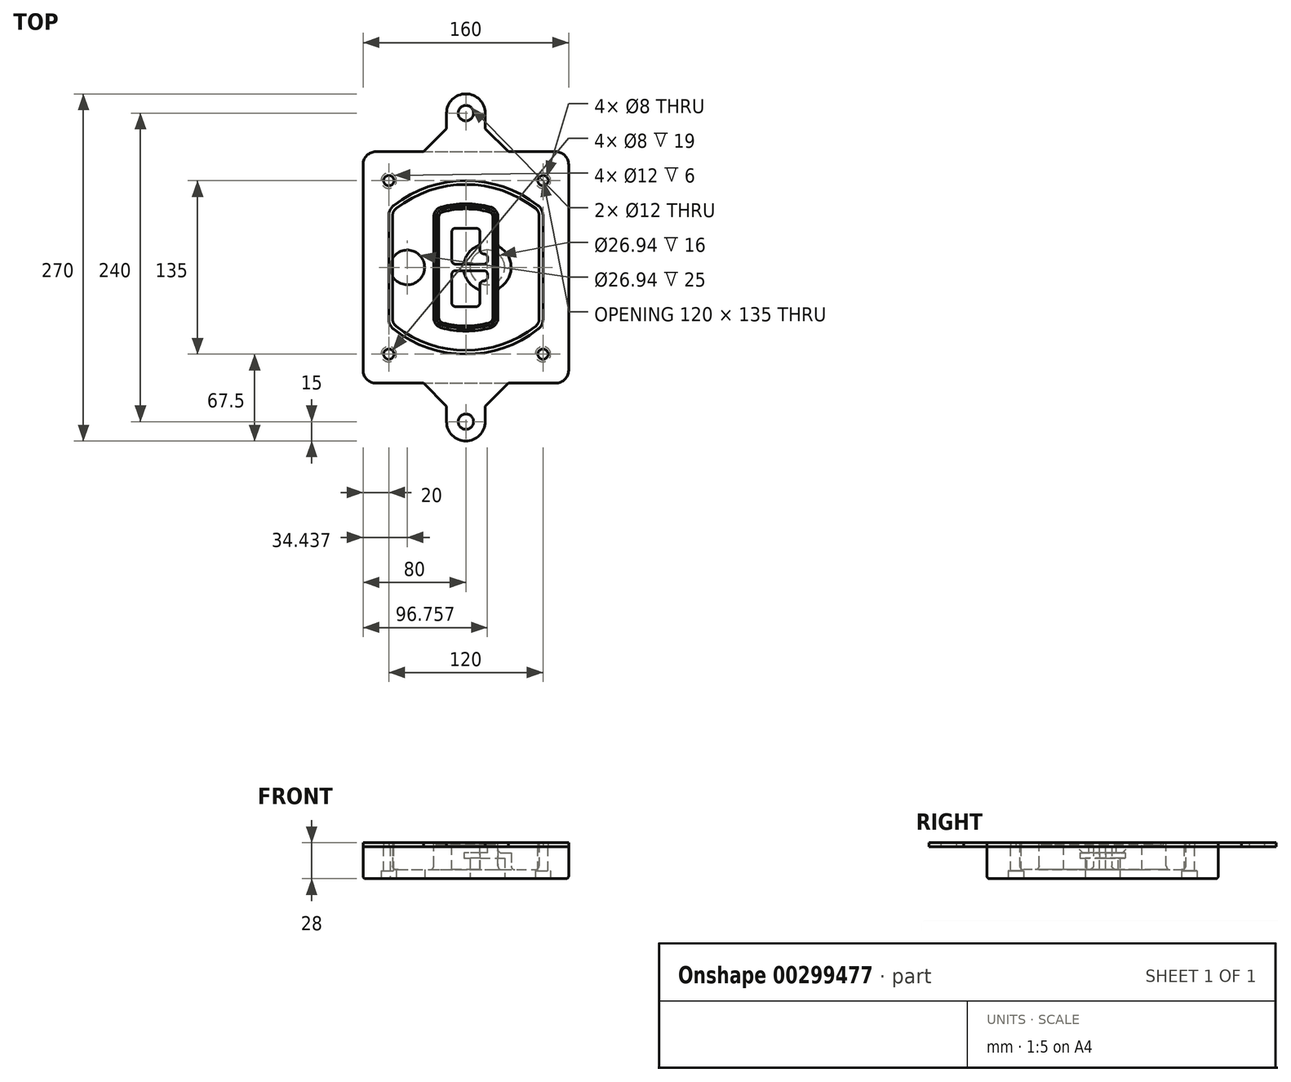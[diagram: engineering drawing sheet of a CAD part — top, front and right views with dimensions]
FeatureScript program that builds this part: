
annotation { "Feature Type Name" : "Feature", "Feature Type Description" : "" }
export const myFeature = defineFeature(function(context is Context, id is Id, definition is map)
    precondition{}
    {
        {
            var Q0;
            Q0=qCreatedBy(makeId("Top.planeOp"),FACE);
            var sketch = newSketch(context, id + "F0", { "sketchPlane" : qUnion([Q0])});
            skPoint(sketch, "E0.rect.middle", {"position": v(0, 0) * mm});
            skLineSegment(sketch, "E1.bottom", {"start": v(-70, -90) * mm, "end": v(70, -90) * mm});
            skLineSegment(sketch, "E1.top", {"start": v(-70, 90) * mm, "end": v(70, 90) * mm});
            skLineSegment(sketch, "E1.left", {"start": v(-80, -80) * mm, "end": v(-80, 80) * mm});
            skLineSegment(sketch, "E1.right", {"start": v(80, -80) * mm, "end": v(80, 80) * mm});
            skLineSegment(sketch, "E2", {"start": v(-80, 90) * mm, "end": v(80, -90) * mm, "construction": true});
            skLineSegment(sketch, "E3", {"start": v(80, 90) * mm, "end": v(-80, -90) * mm, "construction": true});
            skCircle(sketch, "E4", {"center": v(-60, 67.5) * mm, "radius": 4 * mm});
            skCircle(sketch, "E5", {"center": v(60, 67.5) * mm, "radius": 4 * mm});
            skCircle(sketch, "E6", {"center": v(60, -67.5) * mm, "radius": 4 * mm});
            skCircle(sketch, "E7", {"center": v(-60, -67.5) * mm, "radius": 4 * mm});
            skLineSegment(sketch, "E8", {"start": v(-60, 67.5) * mm, "end": v(60, 67.5) * mm, "construction": true});
            skLineSegment(sketch, "E9", {"start": v(60, 67.5) * mm, "end": v(60, -67.5) * mm, "construction": true});
            skLineSegment(sketch, "E10", {"start": v(60, -67.5) * mm, "end": v(-60, -67.5) * mm, "construction": true});
            skLineSegment(sketch, "E11", {"start": v(-60, -67.5) * mm, "end": v(-60, 67.5) * mm, "construction": true});
            skLineSegment(sketch, "E12", {"start": v(-60, 40.3) * mm, "end": v(-60, -40.3) * mm});
            skLineSegment(sketch, "E13", {"start": v(60, 40.3) * mm, "end": v(60, -40.3) * mm});
            skArc(sketch, "E14", {"start": v(56.15, 48.18) * mm, "mid": v(0, 67.5) * mm, "end": v(-56.15, 48.18) * mm});
            skArc(sketch, "E15", {"start": v(-56.15, -48.18) * mm, "mid": v(0, -67.5) * mm, "end": v(56.15, -48.18) * mm});
            skLineSegment(sketch, "E16", {"start": v(-60, 0) * mm, "end": v(60, 0) * mm, "construction": true});
            skPoint(sketch, "E17.visualSharp", {"position": v(-60, -45) * mm});
            skArc(sketch, "E17.filletArc", {"start": v(-60, -40.3) * mm, "mid": v(-58.99, -44.68) * mm, "end": v(-56.15, -48.18) * mm});
            skPoint(sketch, "E18.visualSharp", {"position": v(-60, 45) * mm});
            skArc(sketch, "E18.filletArc", {"start": v(-56.15, 48.18) * mm, "mid": v(-58.99, 44.68) * mm, "end": v(-60, 40.3) * mm});
            skPoint(sketch, "E19.visualSharp", {"position": v(60, 45) * mm});
            skArc(sketch, "E19.filletArc", {"start": v(60, 40.3) * mm, "mid": v(58.99, 44.68) * mm, "end": v(56.15, 48.18) * mm});
            skPoint(sketch, "E20.visualSharp", {"position": v(60, -45) * mm});
            skArc(sketch, "E20.filletArc", {"start": v(56.15, -48.18) * mm, "mid": v(58.99, -44.68) * mm, "end": v(60, -40.3) * mm});
            skPoint(sketch, "E21.visualSharp", {"position": v(-80, 90) * mm});
            skArc(sketch, "E21.filletArc", {"start": v(-70, 90) * mm, "mid": v(-77.07, 87.07) * mm, "end": v(-80, 80) * mm});
            skPoint(sketch, "E22.visualSharp", {"position": v(80, 90) * mm});
            skArc(sketch, "E22.filletArc", {"start": v(80, 80) * mm, "mid": v(77.07, 87.07) * mm, "end": v(70, 90) * mm});
            skPoint(sketch, "E23.visualSharp", {"position": v(80, -90) * mm});
            skArc(sketch, "E23.filletArc", {"start": v(70, -90) * mm, "mid": v(77.07, -87.07) * mm, "end": v(80, -80) * mm});
            skPoint(sketch, "E24.visualSharp", {"position": v(-80, -90) * mm});
            skArc(sketch, "E24.filletArc", {"start": v(-80, -80) * mm, "mid": v(-77.07, -87.07) * mm, "end": v(-70, -90) * mm});
            skArc(sketch, "E25.0", {"start": v(57, 40.3) * mm, "mid": v(56.3, 43.36) * mm, "end": v(54.3, 45.81) * mm});
            skLineSegment(sketch, "E25.1", {"start": v(57, 40.3) * mm, "end": v(57, -40.3) * mm});
            skArc(sketch, "E25.2", {"start": v(54.3, -45.81) * mm, "mid": v(56.3, -43.36) * mm, "end": v(57, -40.3) * mm});
            skArc(sketch, "E25.3", {"start": v(-54.3, -45.81) * mm, "mid": v(0, -64.5) * mm, "end": v(54.3, -45.81) * mm});
            skArc(sketch, "E25.4", {"start": v(-57, -40.3) * mm, "mid": v(-56.3, -43.36) * mm, "end": v(-54.3, -45.81) * mm});
            skArc(sketch, "E25.5", {"start": v(54.3, 45.81) * mm, "mid": v(0, 64.5) * mm, "end": v(-54.3, 45.81) * mm});
            skLineSegment(sketch, "E25.6", {"start": v(-57, 40.3) * mm, "end": v(-57, -40.3) * mm});
            skArc(sketch, "E25.7", {"start": v(-54.3, 45.81) * mm, "mid": v(-56.3, 43.36) * mm, "end": v(-57, 40.3) * mm});
            skArc(sketch, "E26.0", {"start": v(-58.62, 51.33) * mm, "mid": v(-62.58, 46.43) * mm, "end": v(-64, 40.3) * mm});
            skArc(sketch, "E26.1", {"start": v(58.62, 51.33) * mm, "mid": v(0, 71.5) * mm, "end": v(-58.62, 51.33) * mm});
            skArc(sketch, "E26.2", {"start": v(64, 40.3) * mm, "mid": v(62.58, 46.43) * mm, "end": v(58.62, 51.33) * mm});
            skLineSegment(sketch, "E26.3", {"start": v(64, 40.3) * mm, "end": v(64, -40.3) * mm});
            skArc(sketch, "E26.4", {"start": v(58.62, -51.33) * mm, "mid": v(62.58, -46.43) * mm, "end": v(64, -40.3) * mm});
            skLineSegment(sketch, "E26.5", {"start": v(-64, 40.3) * mm, "end": v(-64, -40.3) * mm});
            skArc(sketch, "E26.6", {"start": v(-58.62, -51.33) * mm, "mid": v(0, -71.5) * mm, "end": v(58.62, -51.33) * mm});
            skArc(sketch, "E26.7", {"start": v(-64, -40.3) * mm, "mid": v(-62.58, -46.43) * mm, "end": v(-58.62, -51.33) * mm});
            skSolve(sketch);
        }
        {
            var Q0;
            Q0=makeQuery(id+"F0.imprint","IMPRINT",FACE,{"disambiguationData":[TD([[makeQuery(id+"F0.imprint","IMPRINT",EDGE,{"derivedFrom":sQuery(id+"F0.wireOp",EDGE,"E1.bottom")}),1.0]])]});
            var Q1;
            Q1=makeQuery(id+"F0.imprint","IMPRINT",FACE,{"disambiguationData":[TD([[makeQuery(id+"F0.imprint","IMPRINT",EDGE,{"derivedFrom":sQuery(id+"F0.wireOp",EDGE,"E12")}),1.0]])]});
            var Q2;
            Q2=makeQuery(id+"F0.imprint","IMPRINT",FACE,{"disambiguationData":[TD([[makeQuery(id+"F0.imprint","IMPRINT",EDGE,{"derivedFrom":sQuery(id+"F0.wireOp",EDGE,"E25.0")}),1.0]])]});
            var Q3;
            Q3=makeQuery(id+"F0.imprint","IMPRINT",FACE,{"disambiguationData":[TD([[makeQuery(id+"F0.imprint","IMPRINT",EDGE,{"derivedFrom":sQuery(id+"F0.wireOp",EDGE,"E12")}),-1.0]])]});
            extrude(context, id + "F1", {"entities" : qUnion([Q0, Q1, Q2, Q3]), "oppositeDirection" : true, "depth" : 25 * mm});
        }
        {
            var Q0;
            Q0=makeQuery(id+"F0.imprint","IMPRINT",FACE,{"disambiguationData":[TD([[makeQuery(id+"F0.imprint","IMPRINT",EDGE,{"derivedFrom":sQuery(id+"F0.wireOp",EDGE,"E12")}),1.0]])]});
            extrude(context, id + "F2", {"entities" : qUnion([Q0]), "operationType" : NewBodyOperationType.ADD, "depth" : 3 * mm});
        }
        {
            var Q0;
            Q0=makeQuery(id+"F0.imprint","IMPRINT",FACE,{"disambiguationData":[TD([[makeQuery(id+"F0.imprint","IMPRINT",EDGE,{"derivedFrom":sQuery(id+"F0.wireOp",EDGE,"E25.0")}),1.0]])]});
            extrude(context, id + "F3", {"entities" : qUnion([Q0]), "operationType" : NewBodyOperationType.REMOVE, "oppositeDirection" : true, "depth" : 18 * mm});
        }
        {
            var Q0;
            Q0=makeQuery(id+"F2.opExtrude","CAP_FACE",FACE,{"disambiguationData":[OSD([sQuery(id+"F0.wireOp",EDGE,"E12"),sQuery(id+"F0.wireOp",EDGE,"E13"),sQuery(id+"F0.wireOp",EDGE,"E14"),sQuery(id+"F0.wireOp",EDGE,"E15"),sQuery(id+"F0.wireOp",EDGE,"E17.filletArc"),sQuery(id+"F0.wireOp",EDGE,"E18.filletArc"),sQuery(id+"F0.wireOp",EDGE,"E19.filletArc"),sQuery(id+"F0.wireOp",EDGE,"E20.filletArc"),sQuery(id+"F0.wireOp",EDGE,"E25.0"),sQuery(id+"F0.wireOp",EDGE,"E25.1"),sQuery(id+"F0.wireOp",EDGE,"E25.2"),sQuery(id+"F0.wireOp",EDGE,"E25.3"),sQuery(id+"F0.wireOp",EDGE,"E25.4"),sQuery(id+"F0.wireOp",EDGE,"E25.5"),sQuery(id+"F0.wireOp",EDGE,"E25.6"),sQuery(id+"F0.wireOp",EDGE,"E25.7")])],"isStart":false});
            var sketch = newSketch(context, id + "F4", { "sketchPlane" : qUnion([Q0])});
            skArc(sketch, "E27.0", {"start": v(-19.08, -46.97) * mm, "mid": v(0, -49.5) * mm, "end": v(19.08, -46.97) * mm});
            skArc(sketch, "E28.0", {"start": v(19.08, 46.97) * mm, "mid": v(0, 49.5) * mm, "end": v(-19.08, 46.97) * mm});
            skLineSegment(sketch, "E29", {"start": v(-25, 39.25) * mm, "end": v(-25, -39.25) * mm});
            skLineSegment(sketch, "E30", {"start": v(25, 39.25) * mm, "end": v(25, -39.25) * mm});
            skLineSegment(sketch, "E31", {"start": v(-25, 45.1) * mm, "end": v(25, 45.1) * mm, "construction": true});
            skLineSegment(sketch, "E32", {"start": v(-25, -45.1) * mm, "end": v(25, -45.1) * mm, "construction": true});
            skPoint(sketch, "E33.visualSharp", {"position": v(-25, 45.1) * mm});
            skArc(sketch, "E33.filletArc", {"start": v(-19.08, 46.97) * mm, "mid": v(-23.35, 44.11) * mm, "end": v(-25, 39.25) * mm});
            skPoint(sketch, "E34.visualSharp", {"position": v(25, 45.1) * mm});
            skArc(sketch, "E34.filletArc", {"start": v(25, 39.25) * mm, "mid": v(23.35, 44.11) * mm, "end": v(19.08, 46.97) * mm});
            skPoint(sketch, "E35.visualSharp", {"position": v(25, -45.1) * mm});
            skArc(sketch, "E35.filletArc", {"start": v(19.08, -46.97) * mm, "mid": v(23.35, -44.11) * mm, "end": v(25, -39.25) * mm});
            skPoint(sketch, "E36.visualSharp", {"position": v(-25, -45.1) * mm});
            skArc(sketch, "E36.filletArc", {"start": v(-25, -39.25) * mm, "mid": v(-23.35, -44.11) * mm, "end": v(-19.08, -46.97) * mm});
            skArc(sketch, "E37.0", {"start": v(54.3, 45.81) * mm, "mid": v(0, 64.5) * mm, "end": v(-54.3, 45.81) * mm});
            skArc(sketch, "E37.1", {"start": v(-54.3, 45.81) * mm, "mid": v(-56.3, 43.36) * mm, "end": v(-57, 40.3) * mm});
            skLineSegment(sketch, "E37.2", {"start": v(-57, 40.3) * mm, "end": v(-57, -40.3) * mm});
            skArc(sketch, "E37.3", {"start": v(-57, -40.3) * mm, "mid": v(-56.3, -43.36) * mm, "end": v(-54.3, -45.81) * mm});
            skArc(sketch, "E37.4", {"start": v(-54.3, -45.81) * mm, "mid": v(0, -64.5) * mm, "end": v(54.3, -45.81) * mm});
            skArc(sketch, "E37.5", {"start": v(54.3, -45.81) * mm, "mid": v(56.3, -43.36) * mm, "end": v(57, -40.3) * mm});
            skLineSegment(sketch, "E37.6", {"start": v(57, 40.3) * mm, "end": v(57, -40.3) * mm});
            skArc(sketch, "E37.7", {"start": v(57, 40.3) * mm, "mid": v(56.3, 43.36) * mm, "end": v(54.3, 45.81) * mm});
            skLineSegment(sketch, "E38.0", {"start": v(23, 39.25) * mm, "end": v(23, -39.25) * mm});
            skArc(sketch, "E38.1", {"start": v(18.56, -45.04) * mm, "mid": v(21.76, -42.9) * mm, "end": v(23, -39.25) * mm});
            skArc(sketch, "E38.2", {"start": v(-18.56, -45.04) * mm, "mid": v(0, -47.5) * mm, "end": v(18.56, -45.04) * mm});
            skArc(sketch, "E38.3", {"start": v(-23, -39.25) * mm, "mid": v(-21.76, -42.9) * mm, "end": v(-18.56, -45.04) * mm});
            skLineSegment(sketch, "E38.4", {"start": v(-23, 39.25) * mm, "end": v(-23, -39.25) * mm});
            skArc(sketch, "E38.5", {"start": v(23, 39.25) * mm, "mid": v(21.76, 42.9) * mm, "end": v(18.56, 45.04) * mm});
            skArc(sketch, "E38.6", {"start": v(-18.56, 45.04) * mm, "mid": v(-21.76, 42.9) * mm, "end": v(-23, 39.25) * mm});
            skArc(sketch, "E38.7", {"start": v(18.56, 45.04) * mm, "mid": v(0, 47.5) * mm, "end": v(-18.56, 45.04) * mm});
            skArc(sketch, "E39.0", {"start": v(21, 39.25) * mm, "mid": v(20.18, 41.68) * mm, "end": v(18.04, 43.1) * mm});
            skLineSegment(sketch, "E39.1", {"start": v(21, 39.25) * mm, "end": v(21, -39.25) * mm});
            skArc(sketch, "E39.2", {"start": v(18.04, -43.1) * mm, "mid": v(20.18, -41.68) * mm, "end": v(21, -39.25) * mm});
            skArc(sketch, "E39.3", {"start": v(-18.04, -43.1) * mm, "mid": v(0, -45.5) * mm, "end": v(18.04, -43.1) * mm});
            skArc(sketch, "E39.4", {"start": v(-21, -39.25) * mm, "mid": v(-20.18, -41.68) * mm, "end": v(-18.04, -43.1) * mm});
            skArc(sketch, "E39.5", {"start": v(18.04, 43.1) * mm, "mid": v(0, 45.5) * mm, "end": v(-18.04, 43.1) * mm});
            skLineSegment(sketch, "E39.6", {"start": v(-21, 39.25) * mm, "end": v(-21, -39.25) * mm});
            skArc(sketch, "E39.7", {"start": v(-18.04, 43.1) * mm, "mid": v(-20.18, 41.68) * mm, "end": v(-21, 39.25) * mm});
            skLineSegment(sketch, "E40", {"start": v(-25, 0) * mm, "end": v(25, 0) * mm, "construction": true});
            skLineSegment(sketch, "E41", {"start": v(-11, 5.5) * mm, "end": v(-11, 27.5) * mm});
            skLineSegment(sketch, "E42", {"start": v(-8, 30.5) * mm, "end": v(8, 30.5) * mm});
            skLineSegment(sketch, "E43", {"start": v(11, 27.5) * mm, "end": v(11, 13.5) * mm});
            skLineSegment(sketch, "E44", {"start": v(14, 10.5) * mm, "end": v(14, 10.5) * mm});
            skLineSegment(sketch, "E45", {"start": v(17, 7.5) * mm, "end": v(17, 5.5) * mm});
            skLineSegment(sketch, "E46", {"start": v(14, 2.5) * mm, "end": v(-8, 2.5) * mm});
            skPoint(sketch, "E47.visualSharp", {"position": v(-11, 30.5) * mm});
            skArc(sketch, "E47.filletArc", {"start": v(-8, 30.5) * mm, "mid": v(-10.12, 29.62) * mm, "end": v(-11, 27.5) * mm});
            skPoint(sketch, "E48.visualSharp", {"position": v(11, 30.5) * mm});
            skArc(sketch, "E48.filletArc", {"start": v(11, 27.5) * mm, "mid": v(10.12, 29.62) * mm, "end": v(8, 30.5) * mm});
            skPoint(sketch, "E49.visualSharp", {"position": v(11, 10.5) * mm});
            skArc(sketch, "E49.filletArc", {"start": v(11, 13.5) * mm, "mid": v(11.88, 11.38) * mm, "end": v(14, 10.5) * mm});
            skPoint(sketch, "E50.visualSharp", {"position": v(17, 10.5) * mm});
            skArc(sketch, "E50.filletArc", {"start": v(17, 7.5) * mm, "mid": v(16.12, 9.62) * mm, "end": v(14, 10.5) * mm});
            skPoint(sketch, "E51.visualSharp", {"position": v(17, 2.5) * mm});
            skArc(sketch, "E51.filletArc", {"start": v(14, 2.5) * mm, "mid": v(16.12, 3.38) * mm, "end": v(17, 5.5) * mm});
            skPoint(sketch, "E52.visualSharp", {"position": v(-11, 2.5) * mm});
            skArc(sketch, "E52.filletArc", {"start": v(-11, 5.5) * mm, "mid": v(-10.12, 3.38) * mm, "end": v(-8, 2.5) * mm});
            skLineSegment(sketch, "E53.0.MirrorCS", {"start": v(14, -2.5) * mm, "end": v(-8, -2.5) * mm});
            skArc(sketch, "E54.0.MirrorCS", {"start": v(-11, -5.5) * mm, "mid": v(-10.12, -3.38) * mm, "end": v(-8, -2.5) * mm});
            skLineSegment(sketch, "E55.0.MirrorCS", {"start": v(-11, -5.5) * mm, "end": v(-11, -27.5) * mm});
            skArc(sketch, "E56.0.MirrorCS", {"start": v(-8, -30.5) * mm, "mid": v(-10.12, -29.62) * mm, "end": v(-11, -27.5) * mm});
            skLineSegment(sketch, "E57.0.MirrorCS", {"start": v(-8, -30.5) * mm, "end": v(8, -30.5) * mm});
            skArc(sketch, "E58.0.MirrorCS", {"start": v(11, -27.5) * mm, "mid": v(10.12, -29.62) * mm, "end": v(8, -30.5) * mm});
            skLineSegment(sketch, "E59.0.MirrorCS", {"start": v(11, -27.5) * mm, "end": v(11, -13.5) * mm});
            skArc(sketch, "E60.0.MirrorCS", {"start": v(11, -13.5) * mm, "mid": v(11.88, -11.38) * mm, "end": v(14, -10.5) * mm});
            skArc(sketch, "E61.0.MirrorCS", {"start": v(17, -7.5) * mm, "mid": v(16.12, -9.62) * mm, "end": v(14, -10.5) * mm});
            skLineSegment(sketch, "E62.0.MirrorCS", {"start": v(17, -7.5) * mm, "end": v(17, -5.5) * mm});
            skArc(sketch, "E63.0.MirrorCS", {"start": v(14, -2.5) * mm, "mid": v(16.12, -3.38) * mm, "end": v(17, -5.5) * mm});
            skSolve(sketch);
        }
        {
            var Q0;
            Q0=makeQuery(id+"F4.imprint","IMPRINT",FACE,{"disambiguationData":[TD([[makeQuery(id+"F4.imprint","IMPRINT",EDGE,{"derivedFrom":sQuery(id+"F4.wireOp",EDGE,"E27.0")}),1.0]])]});
            var Q1;
            Q1=makeQuery(id+"F4.imprint","IMPRINT",FACE,{"disambiguationData":[TD([[makeQuery(id+"F4.imprint","IMPRINT",EDGE,{"derivedFrom":sQuery(id+"F4.wireOp",EDGE,"E38.0")}),-1.0]])]});
            var Q2;
            Q2=makeQuery(id+"F4.imprint","IMPRINT",FACE,{"disambiguationData":[TD([[makeQuery(id+"F4.imprint","IMPRINT",EDGE,{"derivedFrom":sQuery(id+"F4.wireOp",EDGE,"E39.0")}),1.0]])]});
            extrude(context, id + "F5", {"entities" : qUnion([Q0, Q1, Q2]), "operationType" : NewBodyOperationType.ADD, "endBound" : BoundingType.UP_TO_NEXT, "oppositeDirection" : true, "depth" : 25 * mm});
        }
        {
            var Q0;
            Q0=makeQuery(id+"F4.imprint","IMPRINT",FACE,{"disambiguationData":[TD([[makeQuery(id+"F4.imprint","IMPRINT",EDGE,{"derivedFrom":sQuery(id+"F4.wireOp",EDGE,"E38.0")}),-1.0]])]});
            extrude(context, id + "F6", {"entities" : qUnion([Q0]), "operationType" : NewBodyOperationType.REMOVE, "oppositeDirection" : true, "depth" : 2 * mm});
        }
        {
            var Q0;
            Q0=makeQuery(id+"F1.opExtrude","CAP_FACE",FACE,{"disambiguationData":[OSD([sQuery(id+"F0.wireOp",EDGE,"E1.bottom"),sQuery(id+"F0.wireOp",EDGE,"E1.top"),sQuery(id+"F0.wireOp",EDGE,"E1.left"),sQuery(id+"F0.wireOp",EDGE,"E1.right"),sQuery(id+"F0.wireOp",EDGE,"E4"),sQuery(id+"F0.wireOp",EDGE,"E5"),sQuery(id+"F0.wireOp",EDGE,"E6"),sQuery(id+"F0.wireOp",EDGE,"E7"),sQuery(id+"F0.wireOp",EDGE,"E21.filletArc"),sQuery(id+"F0.wireOp",EDGE,"E22.filletArc"),sQuery(id+"F0.wireOp",EDGE,"E23.filletArc"),sQuery(id+"F0.wireOp",EDGE,"E24.filletArc")])],"isStart":false});
            var sketch = newSketch(context, id + "F7", { "sketchPlane" : qUnion([Q0])});
            skCircle(sketch, "E64", {"center": v(16.76, 0) * mm, "radius": 13.47 * mm});
            skCircle(sketch, "E65", {"center": v(-45.56, 0) * mm, "radius": 13.47 * mm});
            skLineSegment(sketch, "E66", {"start": v(80, 0) * mm, "end": v(-80, 0) * mm});
            skCircle(sketch, "E67", {"center": v(16.76, 0) * mm, "radius": 18.47 * mm});
            skCircle(sketch, "E68", {"center": v(60, -67.5) * mm, "radius": 6 * mm});
            skCircle(sketch, "E69", {"center": v(-60, -67.5) * mm, "radius": 6 * mm});
            skCircle(sketch, "E70", {"center": v(-60, 67.5) * mm, "radius": 6 * mm});
            skCircle(sketch, "E71", {"center": v(60, 67.5) * mm, "radius": 6 * mm});
            skSolve(sketch);
        }
        {
            var Q0;
            {var subQ1=sQuery(id+"F7.wireOp",EDGE,"E66");var subQ4=sQuery(id+"F7.wireOp",EDGE,"E64");var subQ6=makeQuery(id+"F7.imprint","INTERSECT",VERTEX,{"disambiguationData":[OD(0.0)],"derivedFrom":[subQ4,subQ1]});Q0=makeQuery(id+"F7.imprint","IMPRINT",FACE,{"disambiguationData":[TD([[makeQuery(id+"F7.imprint","IMPRINT",EDGE,{"disambiguationData":[TD([[subQ6,-1.0]])],"derivedFrom":subQ4}),-1.0]])]});}
            var Q1;
            {var subQ0=sQuery(id+"F7.wireOp",EDGE,"E66");var subQ1=sQuery(id+"F7.wireOp",EDGE,"E64");var subQ3=makeQuery(id+"F7.imprint","INTERSECT",VERTEX,{"disambiguationData":[OD(0.0)],"derivedFrom":[subQ1,subQ0]});Q1=makeQuery(id+"F7.imprint","IMPRINT",FACE,{"disambiguationData":[TD([[makeQuery(id+"F7.imprint","IMPRINT",EDGE,{"disambiguationData":[TD([[subQ3,-1.0]])],"derivedFrom":subQ1}),1.0]])]});}
            var Q2;
            {var subQ0=sQuery(id+"F7.wireOp",EDGE,"E66");var subQ1=sQuery(id+"F7.wireOp",EDGE,"E64");var subQ3=makeQuery(id+"F7.imprint","INTERSECT",VERTEX,{"disambiguationData":[OD(0.0)],"derivedFrom":[subQ1,subQ0]});Q2=makeQuery(id+"F7.imprint","IMPRINT",FACE,{"disambiguationData":[TD([[makeQuery(id+"F7.imprint","IMPRINT",EDGE,{"disambiguationData":[TD([[subQ3,1.0]])],"derivedFrom":subQ1}),1.0]])]});}
            var Q3;
            {var subQ1=sQuery(id+"F7.wireOp",EDGE,"E66");var subQ4=sQuery(id+"F7.wireOp",EDGE,"E64");var subQ6=makeQuery(id+"F7.imprint","INTERSECT",VERTEX,{"disambiguationData":[OD(0.0)],"derivedFrom":[subQ4,subQ1]});Q3=makeQuery(id+"F7.imprint","IMPRINT",FACE,{"disambiguationData":[TD([[makeQuery(id+"F7.imprint","IMPRINT",EDGE,{"disambiguationData":[TD([[subQ6,1.0]])],"derivedFrom":subQ4}),-1.0]])]});}
            extrude(context, id + "F8", {"entities" : qUnion([Q0, Q1, Q2, Q3]), "operationType" : NewBodyOperationType.ADD, "oppositeDirection" : true, "depth" : 20 * mm});
        }
        {
            var Q0;
            {var subQ0=sQuery(id+"F7.wireOp",EDGE,"E66");var subQ1=sQuery(id+"F7.wireOp",EDGE,"E64");var subQ3=makeQuery(id+"F7.imprint","INTERSECT",VERTEX,{"disambiguationData":[OD(0.0)],"derivedFrom":[subQ1,subQ0]});Q0=makeQuery(id+"F7.imprint","IMPRINT",FACE,{"disambiguationData":[TD([[makeQuery(id+"F7.imprint","IMPRINT",EDGE,{"disambiguationData":[TD([[subQ3,-1.0]])],"derivedFrom":subQ1}),1.0]])]});}
            var Q1;
            {var subQ0=sQuery(id+"F7.wireOp",EDGE,"E66");var subQ1=sQuery(id+"F7.wireOp",EDGE,"E64");var subQ3=makeQuery(id+"F7.imprint","INTERSECT",VERTEX,{"disambiguationData":[OD(0.0)],"derivedFrom":[subQ1,subQ0]});Q1=makeQuery(id+"F7.imprint","IMPRINT",FACE,{"disambiguationData":[TD([[makeQuery(id+"F7.imprint","IMPRINT",EDGE,{"disambiguationData":[TD([[subQ3,1.0]])],"derivedFrom":subQ1}),1.0]])]});}
            extrude(context, id + "F9", {"entities" : qUnion([Q0, Q1]), "operationType" : NewBodyOperationType.REMOVE, "oppositeDirection" : true, "depth" : 16 * mm});
        }
        {
            var Q0;
            {var subQ0=sQuery(id+"F7.wireOp",EDGE,"E66");var subQ1=sQuery(id+"F7.wireOp",EDGE,"E65");var subQ3=makeQuery(id+"F7.imprint","INTERSECT",VERTEX,{"disambiguationData":[OD(0.0)],"derivedFrom":[subQ1,subQ0]});Q0=makeQuery(id+"F7.imprint","IMPRINT",FACE,{"disambiguationData":[TD([[makeQuery(id+"F7.imprint","IMPRINT",EDGE,{"disambiguationData":[TD([[subQ3,-1.0]])],"derivedFrom":subQ1}),1.0]])]});}
            var Q1;
            {var subQ0=sQuery(id+"F7.wireOp",EDGE,"E66");var subQ1=sQuery(id+"F7.wireOp",EDGE,"E65");var subQ3=makeQuery(id+"F7.imprint","INTERSECT",VERTEX,{"disambiguationData":[OD(0.0)],"derivedFrom":[subQ1,subQ0]});Q1=makeQuery(id+"F7.imprint","IMPRINT",FACE,{"disambiguationData":[TD([[makeQuery(id+"F7.imprint","IMPRINT",EDGE,{"disambiguationData":[TD([[subQ3,1.0]])],"derivedFrom":subQ1}),1.0]])]});}
            extrude(context, id + "F10", {"entities" : qUnion([Q0, Q1]), "operationType" : NewBodyOperationType.REMOVE, "oppositeDirection" : true, "depth" : 25 * mm});
        }
        {
            var Q0;
            Q0=makeQuery(id+"F7.imprint","IMPRINT",FACE,{"disambiguationData":[TD([[makeQuery(id+"F7.imprint","IMPRINT",EDGE,{"derivedFrom":sQuery(id+"F7.wireOp",EDGE,"E68")}),1.0]])]});
            var Q1;
            Q1=makeQuery(id+"F7.imprint","IMPRINT",FACE,{"disambiguationData":[TD([[makeQuery(id+"F7.imprint","IMPRINT",EDGE,{"derivedFrom":makeQuery(id+"F1.opExtrude","CAP_EDGE",EDGE,{"disambiguationData":[OSD([sQuery(id+"F0.wireOp",EDGE,"E5")])],"isStart":false})}),-1.0]])]});
            var Q2;
            Q2=makeQuery(id+"F7.imprint","IMPRINT",FACE,{"disambiguationData":[TD([[makeQuery(id+"F7.imprint","IMPRINT",EDGE,{"derivedFrom":sQuery(id+"F7.wireOp",EDGE,"E69")}),1.0]])]});
            var Q3;
            Q3=makeQuery(id+"F7.imprint","IMPRINT",FACE,{"disambiguationData":[TD([[makeQuery(id+"F7.imprint","IMPRINT",EDGE,{"derivedFrom":makeQuery(id+"F1.opExtrude","CAP_EDGE",EDGE,{"disambiguationData":[OSD([sQuery(id+"F0.wireOp",EDGE,"E4")])],"isStart":false})}),-1.0]])]});
            var Q4;
            Q4=makeQuery(id+"F7.imprint","IMPRINT",FACE,{"disambiguationData":[TD([[makeQuery(id+"F7.imprint","IMPRINT",EDGE,{"derivedFrom":sQuery(id+"F7.wireOp",EDGE,"E70")}),1.0]])]});
            var Q5;
            Q5=makeQuery(id+"F7.imprint","IMPRINT",FACE,{"disambiguationData":[TD([[makeQuery(id+"F7.imprint","IMPRINT",EDGE,{"derivedFrom":makeQuery(id+"F1.opExtrude","CAP_EDGE",EDGE,{"disambiguationData":[OSD([sQuery(id+"F0.wireOp",EDGE,"E7")])],"isStart":false})}),-1.0]])]});
            var Q6;
            Q6=makeQuery(id+"F7.imprint","IMPRINT",FACE,{"disambiguationData":[TD([[makeQuery(id+"F7.imprint","IMPRINT",EDGE,{"derivedFrom":sQuery(id+"F7.wireOp",EDGE,"E71")}),1.0]])]});
            var Q7;
            Q7=makeQuery(id+"F7.imprint","IMPRINT",FACE,{"disambiguationData":[TD([[makeQuery(id+"F7.imprint","IMPRINT",EDGE,{"derivedFrom":makeQuery(id+"F1.opExtrude","CAP_EDGE",EDGE,{"disambiguationData":[OSD([sQuery(id+"F0.wireOp",EDGE,"E6")])],"isStart":false})}),-1.0]])]});
            extrude(context, id + "F11", {"entities" : qUnion([Q0, Q1, Q2, Q3, Q4, Q5, Q6, Q7]), "operationType" : NewBodyOperationType.REMOVE, "oppositeDirection" : true, "depth" : 6 * mm});
        }
        {
            var Q0;
            Q0=makeQuery(id+"F9.boolean.opBoolean","COPY",FACE,{"derivedFrom":makeQuery(id+"F9.opExtrude","CAP_FACE",FACE,{"disambiguationData":[OSD([sQuery(id+"F7.wireOp",EDGE,"E64")])],"isStart":false})});
            var sketch = newSketch(context, id + "F12", { "sketchPlane" : qUnion([Q0])});
            skArc(sketch, "E72.0", {"start": v(11, 17.55) * mm, "mid": v(2.57, 11.82) * mm, "end": v(-1.54, 2.5) * mm});
            skArc(sketch, "E72.1", {"start": v(-1.54, -2.5) * mm, "mid": v(2.57, -11.82) * mm, "end": v(11, -17.55) * mm});
            skLineSegment(sketch, "E73", {"start": v(-1.54, -2.5) * mm, "end": v(14, -2.5) * mm});
            skLineSegment(sketch, "E74.0", {"start": v(14, 2.5) * mm, "end": v(-1.54, 2.5) * mm});
            skArc(sketch, "E74.1", {"start": v(14, 2.5) * mm, "mid": v(16.12, 3.38) * mm, "end": v(17, 5.5) * mm});
            skLineSegment(sketch, "E74.2", {"start": v(17, 7.5) * mm, "end": v(17, 5.5) * mm});
            skArc(sketch, "E74.3", {"start": v(17, 7.5) * mm, "mid": v(16.12, 9.62) * mm, "end": v(14, 10.5) * mm});
            skArc(sketch, "E74.4", {"start": v(11, 13.5) * mm, "mid": v(11.88, 11.38) * mm, "end": v(14, 10.5) * mm});
            skLineSegment(sketch, "E74.5", {"start": v(11, 17.55) * mm, "end": v(11, 13.5) * mm});
            skLineSegment(sketch, "E74.7", {"start": v(14, -2.5) * mm, "end": v(-1.54, -2.5) * mm});
            skArc(sketch, "E74.8", {"start": v(14, -2.5) * mm, "mid": v(16.12, -3.38) * mm, "end": v(17, -5.5) * mm});
            skLineSegment(sketch, "E74.9", {"start": v(17, -7.5) * mm, "end": v(17, -5.5) * mm});
            skArc(sketch, "E74.10", {"start": v(17, -7.5) * mm, "mid": v(16.12, -9.62) * mm, "end": v(14, -10.5) * mm});
            skArc(sketch, "E74.11", {"start": v(11, -13.5) * mm, "mid": v(11.88, -11.38) * mm, "end": v(14, -10.5) * mm});
            skLineSegment(sketch, "E74.12", {"start": v(11, -17.55) * mm, "end": v(11, -13.5) * mm});
            skPoint(sketch, "E75.orphan", {"position": v(11, -27.5) * mm});
            skPoint(sketch, "E76.orphan", {"position": v(-8, -2.5) * mm});
            skPoint(sketch, "E77.orphan", {"position": v(-8, 2.5) * mm});
            skPoint(sketch, "E78.orphan", {"position": v(11, 27.5) * mm});
            skSolve(sketch);
        }
        {
            var Q0;
            {var subQ7=sQuery(id+"F12.wireOp",EDGE,"E72.0");var subQ14=sQuery(id+"F12.wireOp",EDGE,"E72.1");var subQ16=sQuery(id+"F12.wireOp",EDGE,"E74.1");var subQ18=sQuery(id+"F12.wireOp",EDGE,"E74.8");Q0=qUnion([makeQuery(id+"F12.imprint","IMPRINT",FACE,{"disambiguationData":[TD([[makeQuery(id+"F12.imprint","IMPRINT",EDGE,{"derivedFrom":subQ7}),1.0]])]}),makeQuery(id+"F12.imprint","IMPRINT",FACE,{"disambiguationData":[TD([[makeQuery(id+"F12.imprint","IMPRINT",EDGE,{"derivedFrom":subQ14}),1.0]])]}),makeQuery(id+"F12.imprint","IMPRINT",FACE,{"disambiguationData":[TD([[makeQuery(id+"F12.imprint","IMPRINT",EDGE,{"derivedFrom":subQ16}),1.0]])]}),makeQuery(id+"F12.imprint","IMPRINT",FACE,{"disambiguationData":[TD([[makeQuery(id+"F12.imprint","IMPRINT",EDGE,{"derivedFrom":subQ18}),-1.0]])]})]);}
            var Q1;
            Q1=makeQuery(id+"F5.boolean.opBoolean","SPLIT",FACE,{"disambiguationData":[TD([makeQuery(id+"F5.opExtrude","SWEPT_FACE",FACE,{"disambiguationData":[OSD([sQuery(id+"F4.wireOp",EDGE,"E41")])]})])],"derivedFrom":makeQuery(id+"F3.boolean.opBoolean","COPY",FACE,{"derivedFrom":makeQuery(id+"F3.opExtrude","CAP_FACE",FACE,{"disambiguationData":[OSD([sQuery(id+"F0.wireOp",EDGE,"E25.0"),sQuery(id+"F0.wireOp",EDGE,"E25.1"),sQuery(id+"F0.wireOp",EDGE,"E25.2"),sQuery(id+"F0.wireOp",EDGE,"E25.3"),sQuery(id+"F0.wireOp",EDGE,"E25.4"),sQuery(id+"F0.wireOp",EDGE,"E25.5"),sQuery(id+"F0.wireOp",EDGE,"E25.6"),sQuery(id+"F0.wireOp",EDGE,"E25.7")])],"isStart":false})})});
            extrude(context, id + "F13", {"entities" : qUnion([Q0]), "operationType" : NewBodyOperationType.REMOVE, "endBound" : BoundingType.UP_TO_SURFACE, "endBoundEntityFace" : qUnion([Q1]), "depth" : 25 * mm});
        }
        {
            var Q0;
            Q0=makeQuery(id+"F3.boolean.opBoolean","COPY",EDGE,{"derivedFrom":makeQuery(id+"F3.opExtrude","CAP_EDGE",EDGE,{"disambiguationData":[OSD([sQuery(id+"F0.wireOp",EDGE,"E25.6")])],"isStart":false})});
            var Q1;
            Q1=makeQuery(id+"F8.boolean.opBoolean","INTERSECT",EDGE,{"derivedFrom":[makeQuery(id+"F5.opExtrude","SWEPT_FACE",FACE,{"disambiguationData":[OSD([sQuery(id+"F4.wireOp",EDGE,"E30")])]}),makeQuery(id+"F8.opExtrude","CAP_FACE",FACE,{"disambiguationData":[OSD([sQuery(id+"F7.wireOp",EDGE,"E67")])],"isStart":false})]});
            var Q2;
            Q2=makeQuery(id+"F8.boolean.opBoolean","INTERSECT",EDGE,{"disambiguationData":[OD(1.0)],"derivedFrom":[makeQuery(id+"F5.opExtrude","SWEPT_FACE",FACE,{"disambiguationData":[OSD([sQuery(id+"F4.wireOp",EDGE,"E30")])]}),makeQuery(id+"F8.opExtrude","SWEPT_FACE",FACE,{"disambiguationData":[OSD([sQuery(id+"F7.wireOp",EDGE,"E67")])]})]});
            var Q3;
            {var subQ0=sQuery(id+"F4.wireOp",EDGE,"E30");Q3=makeQuery(id+"F8.boolean.opBoolean","SPLIT",EDGE,{"disambiguationData":[TD([makeQuery(id+"F5.opExtrude","SWEPT_FACE",FACE,{"disambiguationData":[OSD([sQuery(id+"F4.wireOp",EDGE,"E35.filletArc")])]})])],"derivedFrom":makeQuery(id+"F5.opExtrude","CAP_EDGE",EDGE,{"disambiguationData":[OSD([subQ0])],"isStart":false})});}
            var Q4;
            {var subQ0=sQuery(id+"F0.wireOp",EDGE,"E25.7");var subQ1=sQuery(id+"F0.wireOp",EDGE,"E25.1");var subQ2=sQuery(id+"F0.wireOp",EDGE,"E25.6");var subQ3=sQuery(id+"F0.wireOp",EDGE,"E25.5");var subQ4=sQuery(id+"F0.wireOp",EDGE,"E25.4");var subQ5=sQuery(id+"F0.wireOp",EDGE,"E25.0");var subQ6=sQuery(id+"F0.wireOp",EDGE,"E25.2");var subQ7=sQuery(id+"F0.wireOp",EDGE,"E25.3");Q4=makeQuery(id+"F8.boolean.opBoolean","INTERSECT",EDGE,{"derivedFrom":[makeQuery(id+"F5.boolean.opBoolean","SPLIT",FACE,{"disambiguationData":[TD([makeQuery(id+"F2.opExtrude","SWEPT_FACE",FACE,{"disambiguationData":[OSD([subQ5])]})])],"derivedFrom":makeQuery(id+"F3.boolean.opBoolean","COPY",FACE,{"derivedFrom":makeQuery(id+"F3.opExtrude","CAP_FACE",FACE,{"disambiguationData":[OSD([subQ5,subQ1,subQ6,subQ7,subQ4,subQ3,subQ2,subQ0])],"isStart":false})})}),makeQuery(id+"F8.opExtrude","SWEPT_FACE",FACE,{"disambiguationData":[OSD([sQuery(id+"F7.wireOp",EDGE,"E67")])]})]});}
            var Q5;
            Q5=makeQuery(id+"F8.boolean.opBoolean","INTERSECT",EDGE,{"disambiguationData":[OD(0.0)],"derivedFrom":[makeQuery(id+"F5.opExtrude","SWEPT_FACE",FACE,{"disambiguationData":[OSD([sQuery(id+"F4.wireOp",EDGE,"E30")])]}),makeQuery(id+"F8.opExtrude","SWEPT_FACE",FACE,{"disambiguationData":[OSD([sQuery(id+"F7.wireOp",EDGE,"E67")])]})]});
            fillet(context, id + "F14", {"entities" : qUnion([Q0, Q1, Q2, Q3, Q4, Q5]), "radius" : 3 * mm, "tangentPropagation" : true, "allowEdgeOverflow" : false});
        }
        {
            var Q0;
            Q0=makeQuery(id+"F1.opExtrude","CAP_EDGE",EDGE,{"disambiguationData":[OSD([sQuery(id+"F0.wireOp",EDGE,"E1.bottom")])],"isStart":false});
            fillet(context, id + "F15", {"entities" : qUnion([Q0]), "radius" : 2 * mm, "tangentPropagation" : true, "allowEdgeOverflow" : false});
        }
        {
            var Q0;
            {var subQ0=sQuery(id+"F0.wireOp",EDGE,"E21.filletArc");var subQ1=sQuery(id+"F0.wireOp",EDGE,"E7");var subQ2=sQuery(id+"F0.wireOp",EDGE,"E6");var subQ3=sQuery(id+"F0.wireOp",EDGE,"E5");var subQ4=sQuery(id+"F0.wireOp",EDGE,"E4");var subQ5=sQuery(id+"F0.wireOp",EDGE,"E22.filletArc");var subQ6=sQuery(id+"F0.wireOp",EDGE,"E1.bottom");var subQ7=sQuery(id+"F0.wireOp",EDGE,"E1.right");var subQ8=sQuery(id+"F0.wireOp",EDGE,"E1.top");var subQ9=sQuery(id+"F0.wireOp",EDGE,"E1.left");var subQ10=sQuery(id+"F0.wireOp",EDGE,"E23.filletArc");var subQ11=sQuery(id+"F0.wireOp",EDGE,"E24.filletArc");Q0=makeQuery(id+"F2.boolean.opBoolean","SPLIT",FACE,{"disambiguationData":[TD([makeQuery(id+"F1.opExtrude","SWEPT_FACE",FACE,{"disambiguationData":[OSD([subQ6])]})])],"derivedFrom":makeQuery(id+"F1.opExtrude","CAP_FACE",FACE,{"disambiguationData":[OSD([subQ6,subQ8,subQ9,subQ7,subQ4,subQ3,subQ2,subQ1,subQ0,subQ5,subQ10,subQ11])],"isStart":true})});}
            var sketch = newSketch(context, id + "F16", { "sketchPlane" : qUnion([Q0])});
            skLineSegment(sketch, "E79", {"start": v(0, 90) * mm, "end": v(0, 120) * mm, "construction": true});
            skCircle(sketch, "E80", {"center": v(0, 120) * mm, "radius": 6 * mm});
            skArc(sketch, "E81", {"start": v(15, 120) * mm, "mid": v(0, 135) * mm, "end": v(-15, 120) * mm});
            skLineSegment(sketch, "E82", {"start": v(-15, 120) * mm, "end": v(-15, 108) * mm});
            skLineSegment(sketch, "E83", {"start": v(15, 120) * mm, "end": v(15, 108) * mm});
            skLineSegment(sketch, "E84", {"start": v(33, 90) * mm, "end": v(15, 108) * mm});
            skLineSegment(sketch, "E85", {"start": v(-33, 90) * mm, "end": v(-15, 108) * mm});
            skLineSegment(sketch, "E86", {"start": v(-80, 0) * mm, "end": v(80, 0) * mm, "construction": true});
            skLineSegment(sketch, "E87.MirrorCS", {"start": v(-33, -90) * mm, "end": v(-15, -108) * mm});
            skLineSegment(sketch, "E88.MirrorCS", {"start": v(-15, -120) * mm, "end": v(-15, -108) * mm});
            skArc(sketch, "E89.MirrorCS", {"start": v(15, -120) * mm, "mid": v(0, -135) * mm, "end": v(-15, -120) * mm});
            skCircle(sketch, "E90.MirrorC", {"center": v(0, -120) * mm, "radius": 6 * mm});
            skLineSegment(sketch, "E91.MirrorCS", {"start": v(0, -90) * mm, "end": v(0, -120) * mm, "construction": true});
            skLineSegment(sketch, "E92.MirrorCS", {"start": v(15, -120) * mm, "end": v(15, -108) * mm});
            skLineSegment(sketch, "E93.MirrorCS", {"start": v(33, -90) * mm, "end": v(15, -108) * mm});
            skSolve(sketch);
        }
        {
            var Q0;
            Q0=makeQuery(id+"F16.imprint","IMPRINT",FACE,{"disambiguationData":[TD([[makeQuery(id+"F16.imprint","IMPRINT",EDGE,{"derivedFrom":sQuery(id+"F16.wireOp",EDGE,"E80")}),-1.0]])]});
            var Q1;
            {var subQ0=sQuery(id+"F16.wireOp",EDGE,"E87.MirrorCS");Q1=makeQuery(id+"F16.imprint","IMPRINT",FACE,{"disambiguationData":[TD([[makeQuery(id+"F16.imprint","IMPRINT",EDGE,{"derivedFrom":subQ0}),1.0]])]});}
            var Q2;
            Q2=makeQuery(id+"F16.imprint","IMPRINT",FACE,{"disambiguationData":[TD([[makeQuery(id+"F16.imprint","IMPRINT",EDGE,{"derivedFrom":makeQuery(id+"F1.opExtrude","CAP_EDGE",EDGE,{"disambiguationData":[OSD([sQuery(id+"F0.wireOp",EDGE,"E1.left")])],"isStart":true})}),-1.0]])]});
            var Q3;
            Q3=makeQuery(id+"F2.opExtrude","CAP_FACE",FACE,{"disambiguationData":[OSD([sQuery(id+"F0.wireOp",EDGE,"E12"),sQuery(id+"F0.wireOp",EDGE,"E13"),sQuery(id+"F0.wireOp",EDGE,"E14"),sQuery(id+"F0.wireOp",EDGE,"E15"),sQuery(id+"F0.wireOp",EDGE,"E17.filletArc"),sQuery(id+"F0.wireOp",EDGE,"E18.filletArc"),sQuery(id+"F0.wireOp",EDGE,"E19.filletArc"),sQuery(id+"F0.wireOp",EDGE,"E20.filletArc"),sQuery(id+"F0.wireOp",EDGE,"E25.0"),sQuery(id+"F0.wireOp",EDGE,"E25.1"),sQuery(id+"F0.wireOp",EDGE,"E25.2"),sQuery(id+"F0.wireOp",EDGE,"E25.3"),sQuery(id+"F0.wireOp",EDGE,"E25.4"),sQuery(id+"F0.wireOp",EDGE,"E25.5"),sQuery(id+"F0.wireOp",EDGE,"E25.6"),sQuery(id+"F0.wireOp",EDGE,"E25.7")])],"isStart":false});
            extrude(context, id + "F17", {"entities" : qUnion([Q0, Q1, Q2]), "endBound" : BoundingType.UP_TO_SURFACE, "endBoundEntityFace" : qUnion([Q3]), "depth" : 25 * mm});
        }
    });
